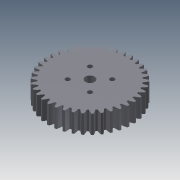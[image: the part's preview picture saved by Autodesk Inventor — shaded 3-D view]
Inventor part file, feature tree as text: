
AUTODESK INVENTOR PART (.ipt)
format: ipt  version: 2015 (Build 190159000, 159)  size: 515,072 bytes
history: native  units: mm (DEFAULTED — no unit token found)
features: other x8, sketch x4, plane x3, extrude x2, projected_geometry x1
ambient origin geometry x8: Origin, YZ Plane, XZ Plane, XY Plane, X Axis, Y Axis, Z Axis, Center Point
bodies: Solid1 (feature_tree)
feature tree (18):
  other  "Blocks"
  extrude  "Extrusion1"  Depth=20.0mm TaperAngle=0.0deg
  plane  "Work Plane2"
  plane  "Work Plane8"
  plane  "Work Plane9"
  other  "Spur Gear"
  extrude  "Extrusion3"  Depth=10.0mm TaperAngle=0.0deg
  sketch  "Sketch4"  dims[d17=0.0mm d34=0.826735mm d39=0.0mm d41=0.0mm d43=70.0mm d46=70.0mm d47=0.0mm d48=0.0mm d51=10.0mm d52=5.0mm d53=15.0mm d54=15.0mm d55=5.0mm d56=12.0mm d57=12.0mm d58=10.0mm d59=0.0mm]
  other  "DXF"
  sketch  "Sketch1"  dims[d0=90.5mm d1=20.0mm d2=0.0mm]
  sketch  "Sketch2"  dims[d3=85.806452mm d4=10.0mm d5=0.0mm]
  other  "Srf1"
  sketch  "Sketch3"  dims[d16=70.0mm]
  projected_geometry  "Projected Loop1"
  other  "Block1"
  other  "Pitch Diameter"
  other  "Block1:1"
  other  "Block1:2"
